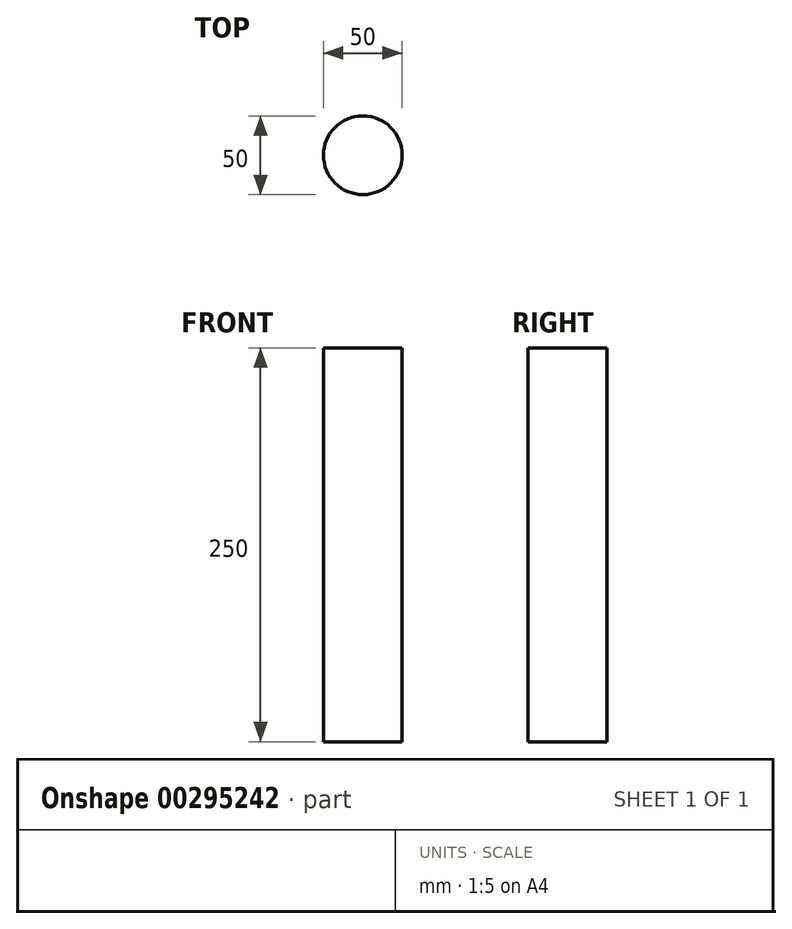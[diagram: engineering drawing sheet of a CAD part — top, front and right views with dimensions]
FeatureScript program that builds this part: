
annotation { "Feature Type Name" : "Feature", "Feature Type Description" : "" }
export const myFeature = defineFeature(function(context is Context, id is Id, definition is map)
    precondition{}
    {
        {
            var Q0;
            Q0=qCreatedBy(makeId("Top.planeOp"),FACE);
            var sketch = newSketch(context, id + "F0", { "sketchPlane" : qUnion([Q0])});
            skCircle(sketch, "E0", {"center": v(0, 0) * mm, "radius": 25 * mm});
            skSolve(sketch);
        }
        {
            var Q0;
            Q0 = qSketchRegion(id + "F0", true);
            extrude(context, id + "F1", {"entities" : qUnion([Q0]), "depth" : 250 * mm});
        }
    });
